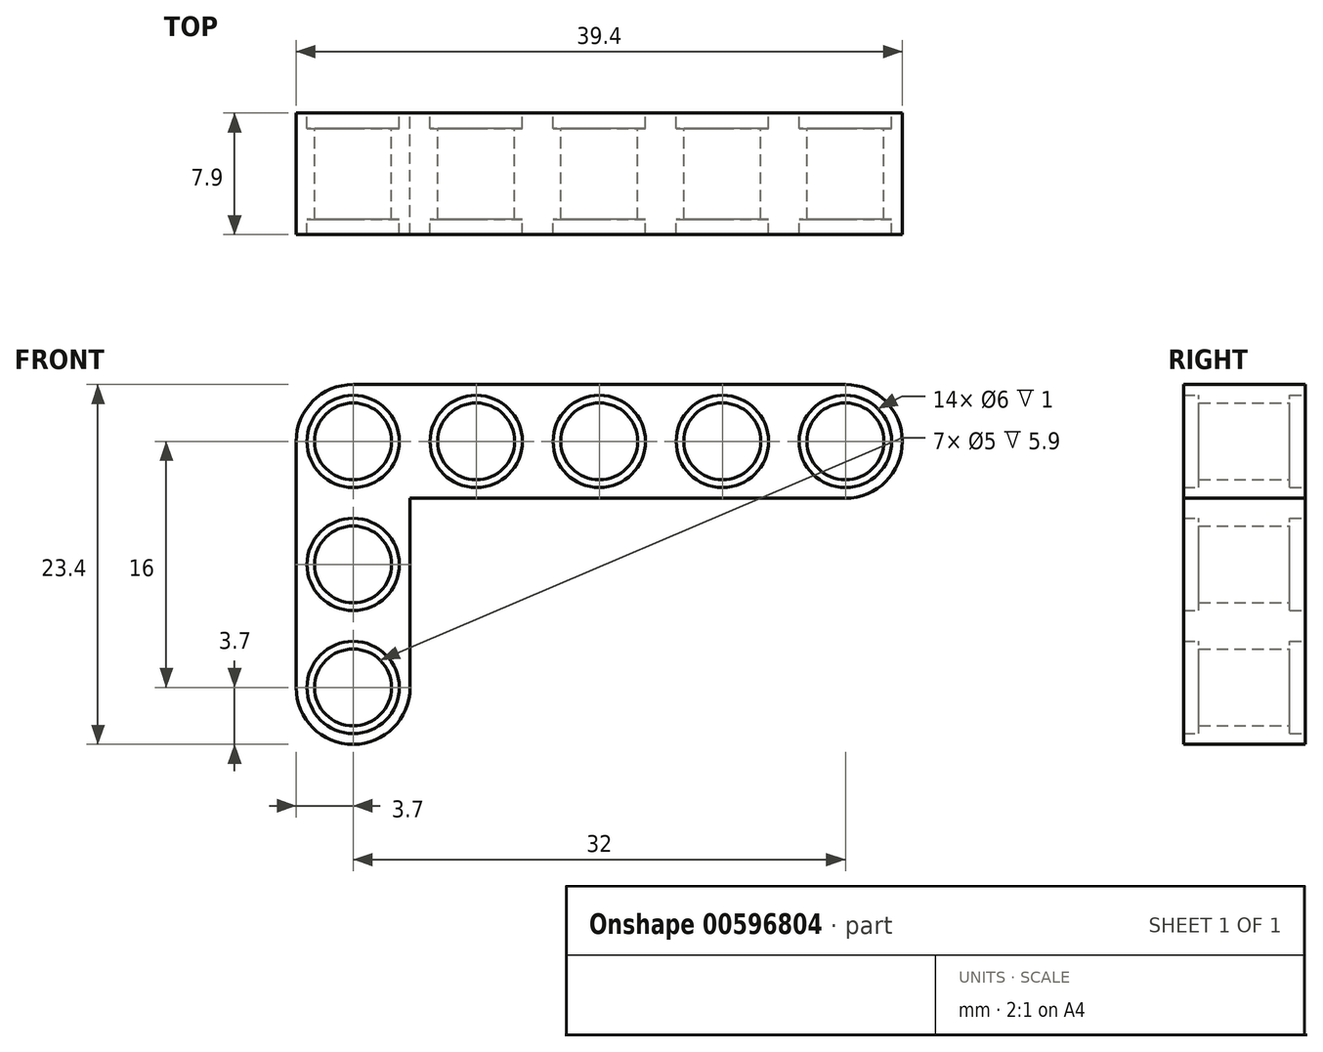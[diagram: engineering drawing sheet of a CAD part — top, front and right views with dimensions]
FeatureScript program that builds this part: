
annotation { "Feature Type Name" : "Feature", "Feature Type Description" : "" }
export const myFeature = defineFeature(function(context is Context, id is Id, definition is map)
    precondition{}
    {
        {
            var Q0;
            Q0=qCreatedBy(makeId("Front.planeOp"),FACE);
            var sketch = newSketch(context, id + "F0", { "sketchPlane" : qUnion([Q0])});
            skLineSegment(sketch, "E0.bottom", {"start": v(19.7, 3.7) * mm, "end": v(-19.7, 3.7) * mm});
            skLineSegment(sketch, "E0.top", {"start": v(19.7, -3.7) * mm, "end": v(-12.3, -3.7) * mm});
            skLineSegment(sketch, "E0.left", {"start": v(19.7, 3.7) * mm, "end": v(19.7, -3.7) * mm});
            skLineSegment(sketch, "E0.right", {"start": v(-19.7, 3.7) * mm, "end": v(-19.7, -3.7) * mm});
            skPoint(sketch, "E0.middle", {"position": v(0, 0) * mm});
            skLineSegment(sketch, "E1.top", {"start": v(-19.7, -19.7) * mm, "end": v(-12.3, -19.7) * mm});
            skLineSegment(sketch, "E1.left", {"start": v(-19.7, -3.7) * mm, "end": v(-19.7, -19.7) * mm});
            skLineSegment(sketch, "E1.right", {"start": v(-12.3, -3.7) * mm, "end": v(-12.3, -19.7) * mm});
            skLineSegment(sketch, "E2.trimOffspring", {"start": v(0, 0) * mm, "end": v(-0.03, 0) * mm, "construction": true});
            skCircle(sketch, "E3", {"center": v(0, 0) * mm, "radius": 3 * mm});
            skCircle(sketch, "E4", {"center": v(0, 0) * mm, "radius": 2.5 * mm});
            skCircle(sketch, "E5", {"center": v(8, 0) * mm, "radius": 2.5 * mm});
            skCircle(sketch, "E6", {"center": v(8, 0) * mm, "radius": 3 * mm});
            skCircle(sketch, "E7", {"center": v(16, 0) * mm, "radius": 2.5 * mm});
            skCircle(sketch, "E8", {"center": v(16, 0) * mm, "radius": 3 * mm});
            skCircle(sketch, "E9", {"center": v(-8, 0) * mm, "radius": 2.5 * mm});
            skCircle(sketch, "E10", {"center": v(-8, 0) * mm, "radius": 3 * mm});
            skCircle(sketch, "E11", {"center": v(-16, 0) * mm, "radius": 2.5 * mm});
            skCircle(sketch, "E12", {"center": v(-16, 0) * mm, "radius": 3 * mm});
            skCircle(sketch, "E13", {"center": v(-16, -8) * mm, "radius": 2.5 * mm});
            skCircle(sketch, "E14", {"center": v(-16, -8) * mm, "radius": 3 * mm});
            skCircle(sketch, "E15", {"center": v(-16, -16) * mm, "radius": 2.5 * mm});
            skCircle(sketch, "E16", {"center": v(-16, -16) * mm, "radius": 3 * mm});
            skSolve(sketch);
        }
        {
            var Q0;
            Q0=qSketchRegion(id+"F0",true);
            extrude(context, id + "F1", {"entities" : qUnion([Q0]), "endBound" : BoundingType.SYMMETRIC, "depth" : 7.9 * mm, "offsetDistance" : 25 * mm});
        }
        {
            var Q0;
            Q0=makeQuery(id+"F0.imprint","IMPRINT",FACE,{"disambiguationData":[TD([[makeQuery(id+"F0.imprint","IMPRINT",EDGE,{"derivedFrom":sQuery(id+"F0.wireOp",EDGE,"E15")}),-1.0]])]});
            var Q1;
            Q1=makeQuery(id+"F0.imprint","IMPRINT",FACE,{"disambiguationData":[TD([[makeQuery(id+"F0.imprint","IMPRINT",EDGE,{"derivedFrom":sQuery(id+"F0.wireOp",EDGE,"E13")}),-1.0]])]});
            var Q2;
            Q2=makeQuery(id+"F0.imprint","IMPRINT",FACE,{"disambiguationData":[TD([[makeQuery(id+"F0.imprint","IMPRINT",EDGE,{"derivedFrom":sQuery(id+"F0.wireOp",EDGE,"E11")}),-1.0]])]});
            var Q3;
            Q3=makeQuery(id+"F0.imprint","IMPRINT",FACE,{"disambiguationData":[TD([[makeQuery(id+"F0.imprint","IMPRINT",EDGE,{"derivedFrom":sQuery(id+"F0.wireOp",EDGE,"E9")}),-1.0]])]});
            var Q4;
            Q4=makeQuery(id+"F0.imprint","IMPRINT",FACE,{"disambiguationData":[TD([[makeQuery(id+"F0.imprint","IMPRINT",EDGE,{"derivedFrom":sQuery(id+"F0.wireOp",EDGE,"E3")}),1.0]])]});
            var Q5;
            Q5=makeQuery(id+"F0.imprint","IMPRINT",FACE,{"disambiguationData":[TD([[makeQuery(id+"F0.imprint","IMPRINT",EDGE,{"derivedFrom":sQuery(id+"F0.wireOp",EDGE,"E5")}),-1.0]])]});
            var Q6;
            Q6=makeQuery(id+"F0.imprint","IMPRINT",FACE,{"disambiguationData":[TD([[makeQuery(id+"F0.imprint","IMPRINT",EDGE,{"derivedFrom":sQuery(id+"F0.wireOp",EDGE,"E7")}),-1.0]])]});
            extrude(context, id + "F2", {"entities" : qUnion([Q0, Q1, Q2, Q3, Q4, Q5, Q6]), "operationType" : NewBodyOperationType.ADD, "endBound" : BoundingType.SYMMETRIC, "depth" : 5.9 * mm, "offsetDistance" : 25 * mm});
        }
        {
            var Q0;
            Q0=makeQuery(id+"F1.opExtrude","SWEPT_EDGE",EDGE,{"disambiguationData":[OSD([sQuery(id+"F0.wireOp",EDGE,"E0.bottom"),sQuery(id+"F0.wireOp",EDGE,"E0.left")])]});
            var Q1;
            Q1=makeQuery(id+"F1.opExtrude","SWEPT_EDGE",EDGE,{"disambiguationData":[OSD([sQuery(id+"F0.wireOp",EDGE,"E0.top"),sQuery(id+"F0.wireOp",EDGE,"E0.left")])]});
            fillet(context, id + "F3", {"entities" : qUnion([Q0, Q1]), "radius" : 3.7 * mm, "tangentPropagation" : true, "allowEdgeOverflow" : false});
        }
        {
            var Q0;
            Q0=makeQuery(id+"F1.opExtrude","CAP_FACE",FACE,{"disambiguationData":[OSD([sQuery(id+"F0.wireOp",EDGE,"E0.bottom"),sQuery(id+"F0.wireOp",EDGE,"E0.top"),sQuery(id+"F0.wireOp",EDGE,"E0.left"),sQuery(id+"F0.wireOp",EDGE,"E0.right"),sQuery(id+"F0.wireOp",EDGE,"E1.top"),sQuery(id+"F0.wireOp",EDGE,"E1.left"),sQuery(id+"F0.wireOp",EDGE,"E1.right"),sQuery(id+"F0.wireOp",EDGE,"E3"),sQuery(id+"F0.wireOp",EDGE,"E6"),sQuery(id+"F0.wireOp",EDGE,"E8"),sQuery(id+"F0.wireOp",EDGE,"E10"),sQuery(id+"F0.wireOp",EDGE,"E12"),sQuery(id+"F0.wireOp",EDGE,"E14"),sQuery(id+"F0.wireOp",EDGE,"E16")])],"isStart":false});
            var sketch = newSketch(context, id + "F4", { "sketchPlane" : qUnion([Q0])});
            skLineSegment(sketch, "E17.bottom", {"start": v(-12.3, -3.7) * mm, "end": v(-19.7, -3.7) * mm});
            skLineSegment(sketch, "E17.top", {"start": v(-12.3, -19.7) * mm, "end": v(-19.7, -19.7) * mm});
            skLineSegment(sketch, "E17.left", {"start": v(-12.3, -3.7) * mm, "end": v(-12.3, -19.7) * mm});
            skLineSegment(sketch, "E17.right", {"start": v(-19.7, -3.7) * mm, "end": v(-19.7, -19.7) * mm});
            skLineSegment(sketch, "E18.bottom", {"start": v(-19.7, -19.7) * mm, "end": v(-27.1, -19.7) * mm});
            skLineSegment(sketch, "E18.top", {"start": v(-19.7, -12.3) * mm, "end": v(-27.1, -12.3) * mm});
            skLineSegment(sketch, "E18.right", {"start": v(-27.1, -19.7) * mm, "end": v(-27.1, -12.3) * mm});
            skCircle(sketch, "E19", {"center": v(-16, -8) * mm, "radius": 2.5 * mm});
            skCircle(sketch, "E20", {"center": v(-16, -16) * mm, "radius": 2.5 * mm});
            skCircle(sketch, "E21", {"center": v(-16, -16) * mm, "radius": 3 * mm});
            skCircle(sketch, "E22", {"center": v(-16, -8) * mm, "radius": 3 * mm});
            skSolve(sketch);
        }
        {
            var Q0;
            Q0=qSketchRegion(id+"F4",true);
            extrude(context, id + "F5", {"entities" : qUnion([Q0]), "depth" : 7.9 * mm, "offsetDistance" : 25 * mm});
        }
        {
            var Q0;
            Q0=makeQuery(id+"F5.opExtrude","SWEPT_BODY",BODY,{"disambiguationData":[OSD([sQuery(id+"F4.wireOp",EDGE,"E17.bottom"),sQuery(id+"F4.wireOp",EDGE,"E17.top"),sQuery(id+"F4.wireOp",EDGE,"E17.left"),sQuery(id+"F4.wireOp",EDGE,"E17.right"),sQuery(id+"F4.wireOp",EDGE,"E18.bottom"),sQuery(id+"F4.wireOp",EDGE,"E18.top"),sQuery(id+"F4.wireOp",EDGE,"E18.right"),sQuery(id+"F4.wireOp",EDGE,"E21"),sQuery(id+"F4.wireOp",EDGE,"E22")])]});
            deleteBodies(context, id + "F6", {"entities" : qUnion([Q0])});
        }
        {
            var Q0;
            Q0=makeQuery(id+"F1.opExtrude","SWEPT_EDGE",EDGE,{"disambiguationData":[OSD([sQuery(id+"F0.wireOp",EDGE,"E1.top"),sQuery(id+"F0.wireOp",EDGE,"E1.right")])]});
            var Q1;
            Q1=makeQuery(id+"F1.opExtrude","SWEPT_EDGE",EDGE,{"disambiguationData":[OSD([sQuery(id+"F0.wireOp",EDGE,"E1.top"),sQuery(id+"F0.wireOp",EDGE,"E1.left")])]});
            fillet(context, id + "F7", {"entities" : qUnion([Q0, Q1]), "radius" : 3.7 * mm, "tangentPropagation" : true, "allowEdgeOverflow" : false});
        }
        {
            var Q0;
            Q0=makeQuery(id+"F1.opExtrude","SWEPT_EDGE",EDGE,{"disambiguationData":[OSD([sQuery(id+"F0.wireOp",EDGE,"E0.bottom"),sQuery(id+"F0.wireOp",EDGE,"E0.right")])]});
            fillet(context, id + "F8", {"entities" : qUnion([Q0]), "radius" : 3.7 * mm, "tangentPropagation" : true, "allowEdgeOverflow" : false});
        }
    });
